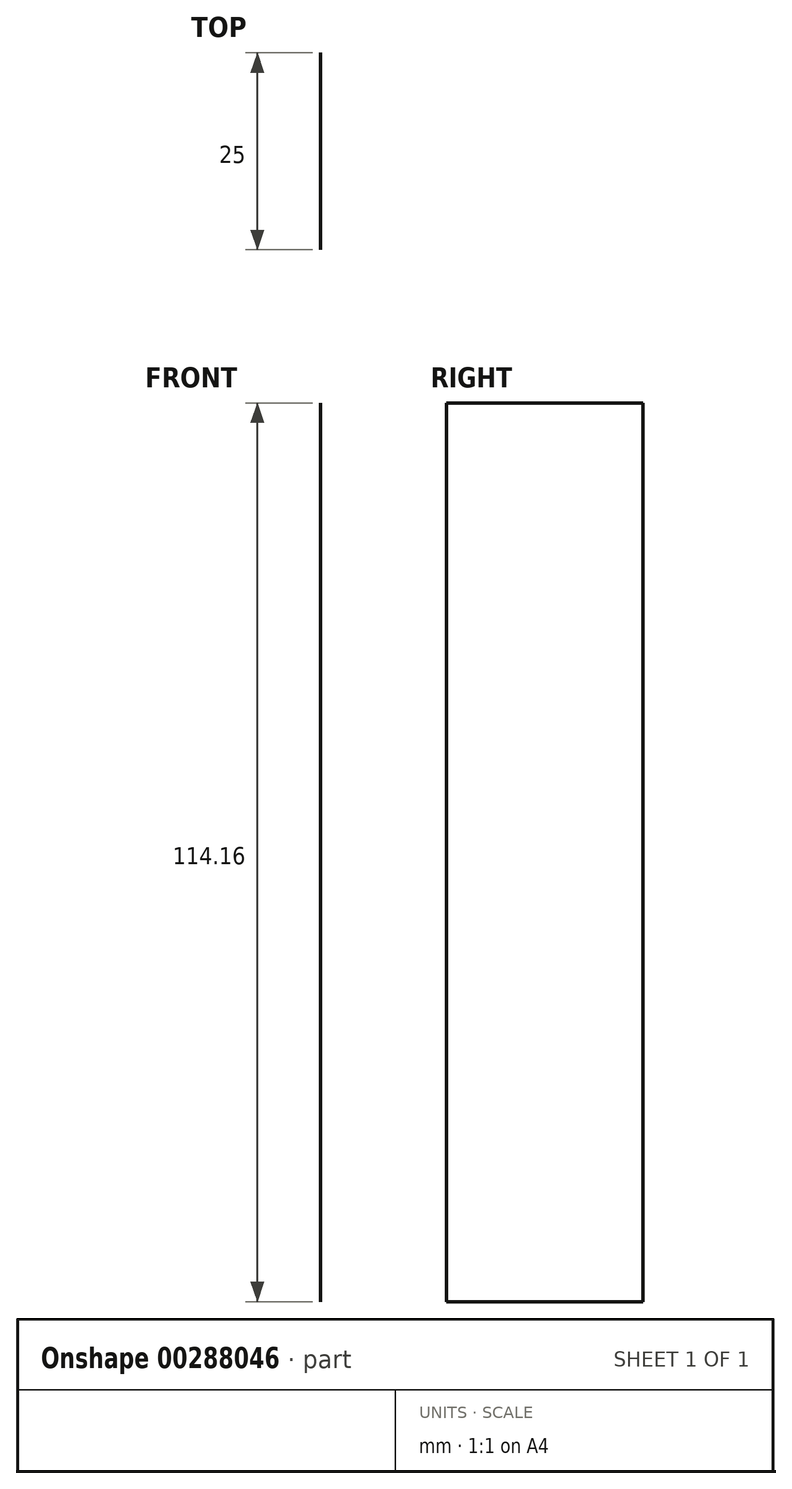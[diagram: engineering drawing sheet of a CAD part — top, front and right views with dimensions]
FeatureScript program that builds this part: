
annotation { "Feature Type Name" : "Feature", "Feature Type Description" : "" }
export const myFeature = defineFeature(function(context is Context, id is Id, definition is map)
    precondition{}
    {
        {
            var Q0;
            Q0=qCreatedBy(makeId("Front.planeOp"),FACE);
            var sketch = newSketch(context, id + "F0", { "sketchPlane" : qUnion([Q0])});
            skLineSegment(sketch, "E0", {"start": v(0, 0) * mm, "end": v(42.29, 0) * mm});
            skLineSegment(sketch, "E1", {"start": v(42.29, 0) * mm, "end": v(42.29, 114.16) * mm});
            skLineSegment(sketch, "E2", {"start": v(42.29, 114.16) * mm, "end": v(0, 0) * mm});
            skSolve(sketch);
        }
        {
            var Q0;
            Q0=sQuery(id+"F0.wireOp",EDGE,"E1");
            extrude(context, id + "F1", {"bodyType" : ToolBodyType.SURFACE, "surfaceEntities" : qUnion([Q0]), "depth" : 25 * mm});
        }
    });
